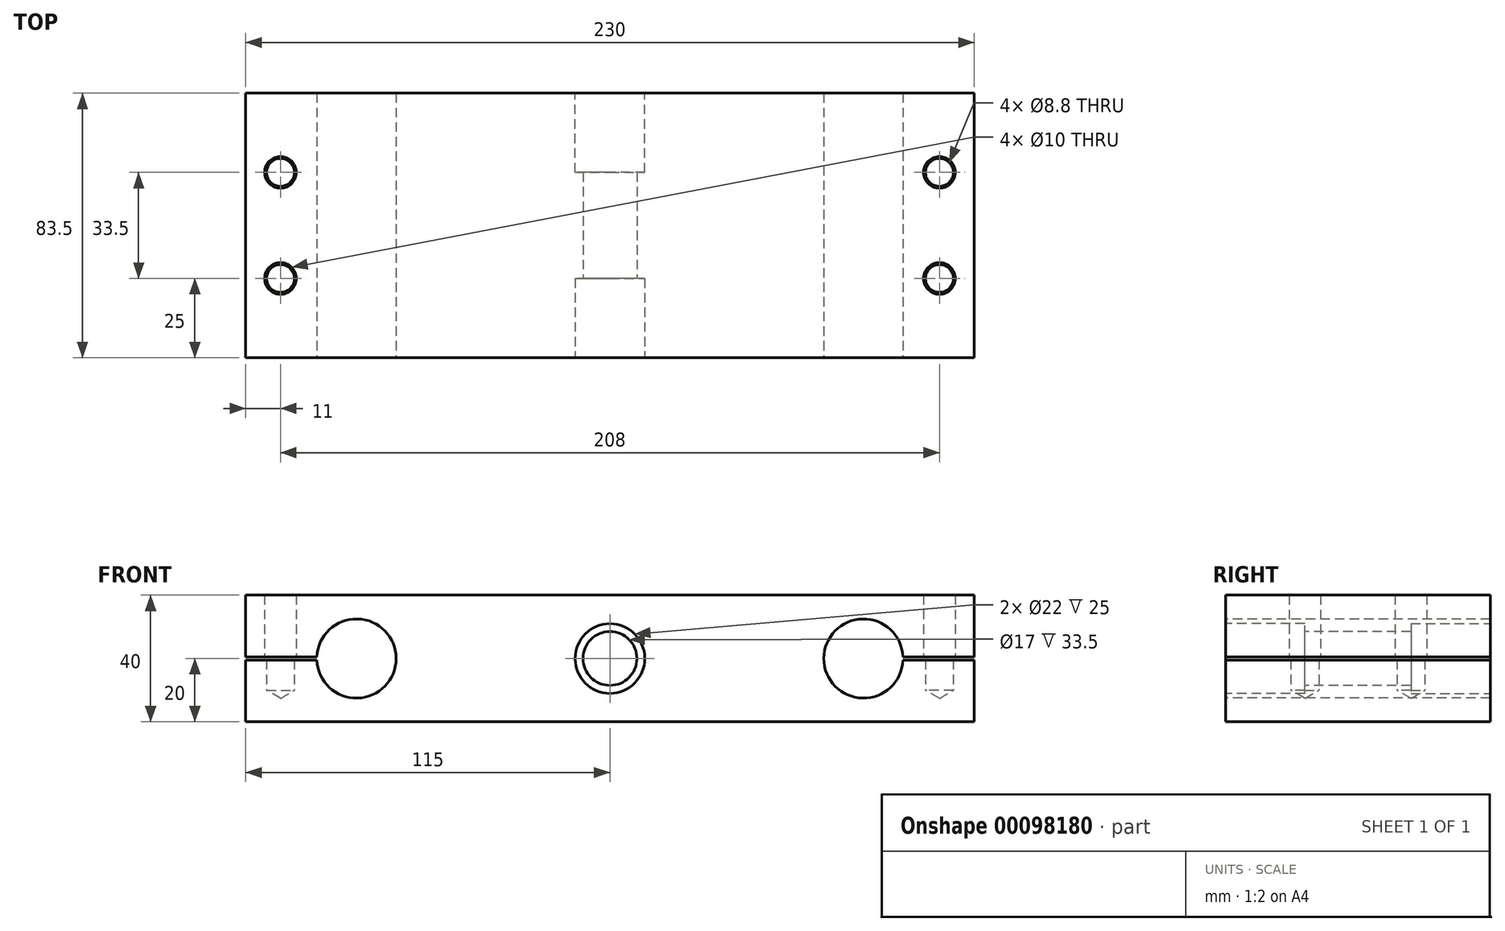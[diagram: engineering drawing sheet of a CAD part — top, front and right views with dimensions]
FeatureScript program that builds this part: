
annotation { "Feature Type Name" : "Feature", "Feature Type Description" : "" }
export const myFeature = defineFeature(function(context is Context, id is Id, definition is map)
    precondition{}
    {
        {
            var Q0;
            Q0=qCreatedBy(makeId("Front.planeOp"),FACE);
            var sketch = newSketch(context, id + "F0", { "sketchPlane" : qUnion([Q0])});
            skLineSegment(sketch, "E0.bottom", {"start": v(0, 0) * mm, "end": v(230, 0) * mm});
            skLineSegment(sketch, "E0.top", {"start": v(0, 40) * mm, "end": v(230, 40) * mm});
            skLineSegment(sketch, "E0.left", {"start": v(0, 0) * mm, "end": v(0, 40) * mm});
            skLineSegment(sketch, "E0.right", {"start": v(230, 0) * mm, "end": v(230, 40) * mm});
            skSolve(sketch);
        }
        {
            var Q0;
            Q0 = qSketchRegion(id + "F0", true);
            extrude(context, id + "F1", {"entities" : qUnion([Q0]), "depth" : 83.5 * mm});
        }
        {
            var Q0;
            Q0=makeQuery(id+"F1.opExtrude","CAP_FACE",FACE,{"disambiguationData":[OSD([sQuery(id+"F0.wireOp",EDGE,"E0.bottom"),sQuery(id+"F0.wireOp",EDGE,"E0.top"),sQuery(id+"F0.wireOp",EDGE,"E0.left"),sQuery(id+"F0.wireOp",EDGE,"E0.right")])],"isStart":false});
            var sketch = newSketch(context, id + "F2", { "sketchPlane" : qUnion([Q0])});
            skLineSegment(sketch, "E1", {"start": v(0, 20) * mm, "end": v(230, 20) * mm});
            skLineSegment(sketch, "E2", {"start": v(115, 40) * mm, "end": v(115, 0) * mm});
            skLineSegment(sketch, "E3", {"start": v(115, 20) * mm, "end": v(195, 20) * mm});
            skLineSegment(sketch, "E4", {"start": v(115, 20) * mm, "end": v(35, 20) * mm});
            skCircle(sketch, "E5", {"center": v(35, 20) * mm, "radius": 12.5 * mm});
            skCircle(sketch, "E6", {"center": v(195, 20) * mm, "radius": 12.5 * mm});
            skCircle(sketch, "E7", {"center": v(115, 20) * mm, "radius": 8.5 * mm});
            skSolve(sketch);
        }
        {
            var Q0;
            Q0 = qSketchRegion(id + "F2", true);
            extrude(context, id + "F3", {"entities" : qUnion([Q0]), "operationType" : NewBodyOperationType.REMOVE, "endBound" : BoundingType.THROUGH_ALL, "oppositeDirection" : true, "depth" : 25 * mm});
        }
        {
            var Q0;
            Q0=makeQuery(id+"F1.opExtrude","CAP_FACE",FACE,{"disambiguationData":[OSD([sQuery(id+"F0.wireOp",EDGE,"E0.bottom"),sQuery(id+"F0.wireOp",EDGE,"E0.top"),sQuery(id+"F0.wireOp",EDGE,"E0.left"),sQuery(id+"F0.wireOp",EDGE,"E0.right")])],"isStart":false});
            var sketch = newSketch(context, id + "F4", { "sketchPlane" : qUnion([Q0])});
            skCircle(sketch, "E8", {"center": v(115, 20) * mm, "radius": 11 * mm});
            skSolve(sketch);
        }
        {
            var Q0;
            Q0 = qSketchRegion(id + "F4", true);
            extrude(context, id + "F5", {"entities" : qUnion([Q0]), "operationType" : NewBodyOperationType.REMOVE, "oppositeDirection" : true, "depth" : 25 * mm});
        }
        {
            var Q0;
            Q0=makeQuery(id+"F1.opExtrude","CAP_FACE",FACE,{"disambiguationData":[OSD([sQuery(id+"F0.wireOp",EDGE,"E0.bottom"),sQuery(id+"F0.wireOp",EDGE,"E0.top"),sQuery(id+"F0.wireOp",EDGE,"E0.left"),sQuery(id+"F0.wireOp",EDGE,"E0.right")])],"isStart":true});
            var sketch = newSketch(context, id + "F6", { "sketchPlane" : qUnion([Q0])});
            skCircle(sketch, "E9", {"center": v(-115, 20) * mm, "radius": 11 * mm});
            skSolve(sketch);
        }
        {
            var Q0;
            Q0 = qSketchRegion(id + "F6", true);
            extrude(context, id + "F7", {"entities" : qUnion([Q0]), "operationType" : NewBodyOperationType.REMOVE, "oppositeDirection" : true, "depth" : 25 * mm});
        }
        {
            var Q0;
            Q0=makeQuery(id+"F1.opExtrude","CAP_FACE",FACE,{"disambiguationData":[OSD([sQuery(id+"F0.wireOp",EDGE,"E0.bottom"),sQuery(id+"F0.wireOp",EDGE,"E0.top"),sQuery(id+"F0.wireOp",EDGE,"E0.left"),sQuery(id+"F0.wireOp",EDGE,"E0.right")])],"isStart":false});
            var sketch = newSketch(context, id + "F8", { "sketchPlane" : qUnion([Q0])});
            skLineSegment(sketch, "E10", {"start": v(0, 20) * mm, "end": v(26.3, 20) * mm});
            skLineSegment(sketch, "E11", {"start": v(230, 20) * mm, "end": v(198.52, 20) * mm});
            skLineSegment(sketch, "E12.0", {"start": v(0, 19.5) * mm, "end": v(26.3, 19.5) * mm});
            skLineSegment(sketch, "E13.0", {"start": v(0, 20.5) * mm, "end": v(26.3, 20.5) * mm});
            skLineSegment(sketch, "E14.0", {"start": v(230, 20.5) * mm, "end": v(198.52, 20.5) * mm});
            skLineSegment(sketch, "E15.0", {"start": v(230, 19.5) * mm, "end": v(198.52, 19.5) * mm});
            skLineSegment(sketch, "E16", {"start": v(198.52, 20.5) * mm, "end": v(198.52, 19.5) * mm});
            skLineSegment(sketch, "E17", {"start": v(230, 20.5) * mm, "end": v(230, 19.5) * mm});
            skLineSegment(sketch, "E18", {"start": v(26.3, 20.5) * mm, "end": v(26.3, 19.5) * mm});
            skLineSegment(sketch, "E19", {"start": v(0, 19.5) * mm, "end": v(0, 20.5) * mm});
            skSolve(sketch);
        }
        {
            var Q0;
            Q0 = qSketchRegion(id + "F8", true);
            extrude(context, id + "F9", {"entities" : qUnion([Q0]), "operationType" : NewBodyOperationType.REMOVE, "endBound" : BoundingType.THROUGH_ALL, "oppositeDirection" : true, "depth" : 25 * mm});
        }
        {
            var Q0;
            Q0=makeQuery(id+"F1.opExtrude","SWEPT_FACE",FACE,{"disambiguationData":[OSD([sQuery(id+"F0.wireOp",EDGE,"E0.top")])]});
            var sketch = newSketch(context, id + "F10", { "sketchPlane" : qUnion([Q0])});
            skLineSegment(sketch, "E20.0", {"start": v(11, -83.5) * mm, "end": v(11, 0) * mm});
            skLineSegment(sketch, "E21.0", {"start": v(0, -25) * mm, "end": v(230, -25) * mm});
            skLineSegment(sketch, "E22.0", {"start": v(0, -58.5) * mm, "end": v(230, -58.5) * mm});
            skLineSegment(sketch, "E23.0", {"start": v(219, -83.5) * mm, "end": v(219, 0) * mm});
            skPoint(sketch, "E24", {"position": v(11, -25) * mm});
            skPoint(sketch, "E25", {"position": v(11, -58.5) * mm});
            skPoint(sketch, "E26", {"position": v(219, -58.5) * mm});
            skPoint(sketch, "E27", {"position": v(219, -25) * mm});
            skSolve(sketch);
        }
        {
            var Q0;
            Q0=sQuery(id+"F10.wireOp",VERTEX,"E24");
            var Q1;
            Q1=sQuery(id+"F10.wireOp",VERTEX,"E25");
            var Q2;
            Q2=sQuery(id+"F10.wireOp",VERTEX,"E27");
            var Q3;
            Q3=sQuery(id+"F10.wireOp",VERTEX,"E26");
            var Q4;
            Q4=makeQuery(id+"F1.opExtrude","SWEPT_BODY",BODY,{"disambiguationData":[OSD([sQuery(id+"F0.wireOp",EDGE,"E0.bottom"),sQuery(id+"F0.wireOp",EDGE,"E0.top"),sQuery(id+"F0.wireOp",EDGE,"E0.left"),sQuery(id+"F0.wireOp",EDGE,"E0.right")])]});
            hole(context, id + "F11", {"style" : HoleStyle.C_BORE, "endStyle" : HoleEndStyle.BLIND, "holeDiameter" : 8.8 * mm, "cBoreDiameter" : 10 * mm, "cBoreDepth" : 20 * mm, "holeDepth" : 30 * mm, "locations" : qUnion([Q0, Q1, Q2, Q3]), "scope" : qUnion([Q4]), "startStyle" : HoleStartStyle.PART});
        }
    });
